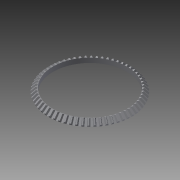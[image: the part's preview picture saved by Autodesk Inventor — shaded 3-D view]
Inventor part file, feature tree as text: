
AUTODESK INVENTOR PART (.ipt)
format: ipt  version: 2015 (Build 190159000, 159)  size: 616,960 bytes
history: native  units: in
note: dims shown in document units (in); Inventor stores cm internally (conversion verified against a paired STEP export)
features: extrude x3, sketch x3, pattern_circular x2, chamfer x1
ambient origin geometry x8: Origin, YZ Plane, XZ Plane, XY Plane, X Axis, Y Axis, Z Axis, Center Point
bodies: Body1 (feature_tree)
feature tree (9):
  extrude  "Extrusion12"  Depth=0.75in
  chamfer  "Chamfer1"  Distance=0.75in
  pattern_circular  "Circular Pattern5"  Count=60 Angle=360.0deg
  extrude  "Extrusion13"  Depth=0.25in
  extrude  "Extrusion14"  Depth=0.25in TaperAngle=0.0deg
  pattern_circular  "Circular Pattern6"  Count=60 Angle=360.0deg
  sketch  "Sketch15"  dims[d52=6.75in d54=0.0412in d55=0.75in d56=0.0in]
  sketch  "Sketch16"  dims[d57=0.75in d58=0.125in d59=45.0deg d60=23.622in d61=360.0deg]
  sketch  "Sketch17"  dims[d63=0.25in d64=-0.1622in d65=12.0in d66=0.25in d67=0.0in d68=23.622in d69=360.0deg]
